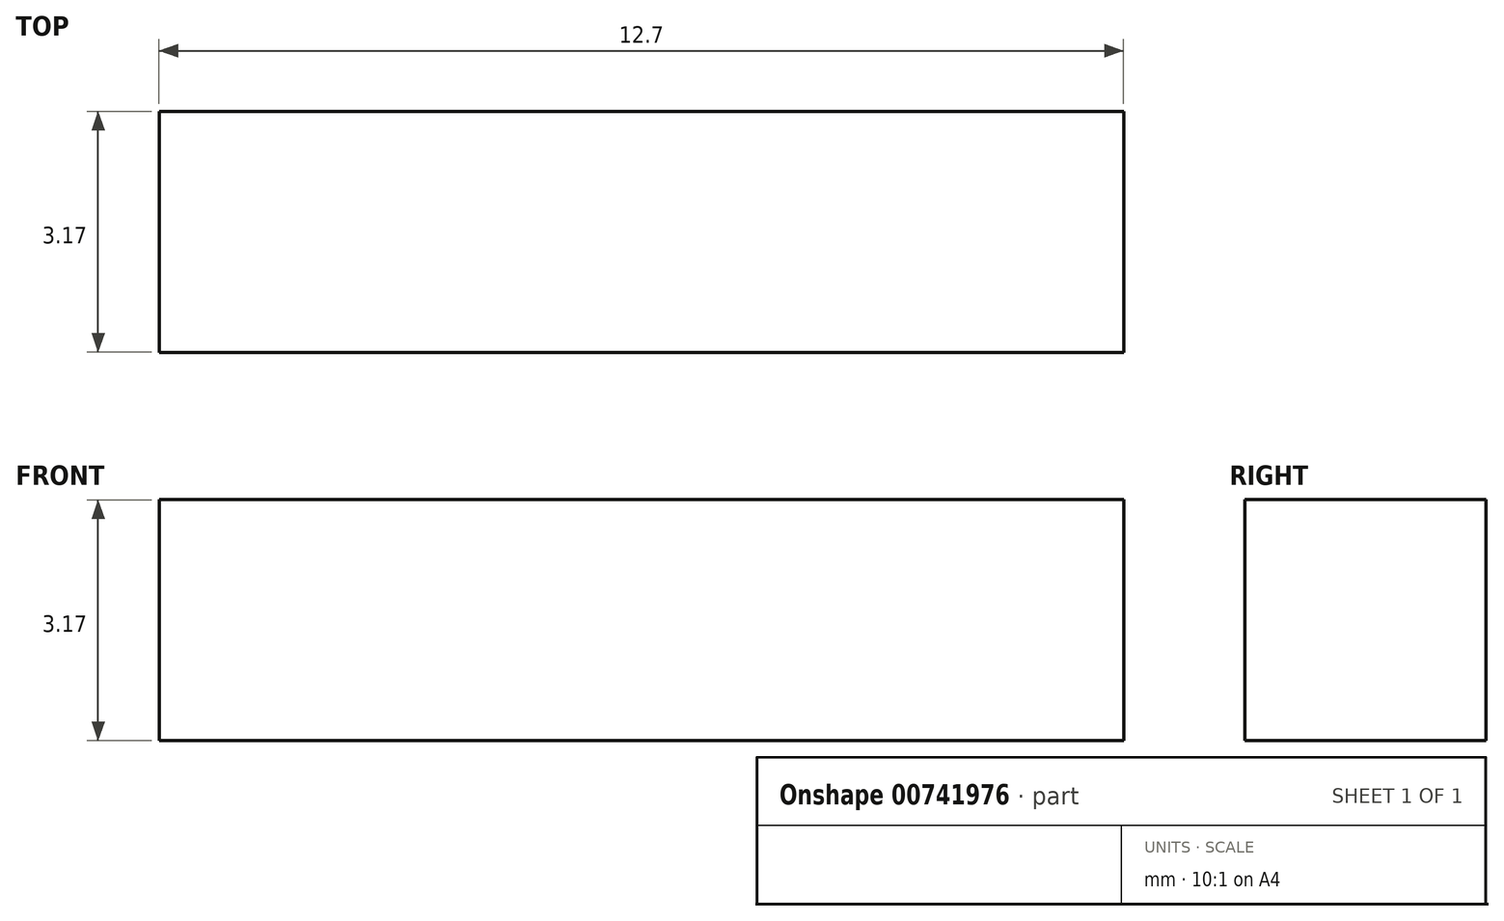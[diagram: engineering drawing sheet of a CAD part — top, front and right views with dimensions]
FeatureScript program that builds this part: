
annotation { "Feature Type Name" : "Feature", "Feature Type Description" : "" }
export const myFeature = defineFeature(function(context is Context, id is Id, definition is map)
    precondition{}
    {
        {
            var Q0;
            Q0=qCreatedBy(makeId("Front.planeOp"),FACE);
            var sketch = newSketch(context, id + "F0", { "sketchPlane" : qUnion([Q0])});
            skLineSegment(sketch, "E0.bottom", {"start": v(2.24, -31.04) * mm, "end": v(14.94, -31.04) * mm});
            skLineSegment(sketch, "E0.top", {"start": v(2.24, -34.21) * mm, "end": v(14.94, -34.21) * mm});
            skLineSegment(sketch, "E0.left", {"start": v(2.24, -31.04) * mm, "end": v(2.24, -34.21) * mm});
            skLineSegment(sketch, "E0.right", {"start": v(14.94, -31.04) * mm, "end": v(14.94, -34.21) * mm});
            skSolve(sketch);
        }
        {
            var Q0;
            Q0 = qSketchRegion(id + "F0", true);
            extrude(context, id + "F1", {"entities" : qUnion([Q0]), "depth" : 3.17 * mm, "offsetDistance" : 25.4 * mm});
        }
    });
